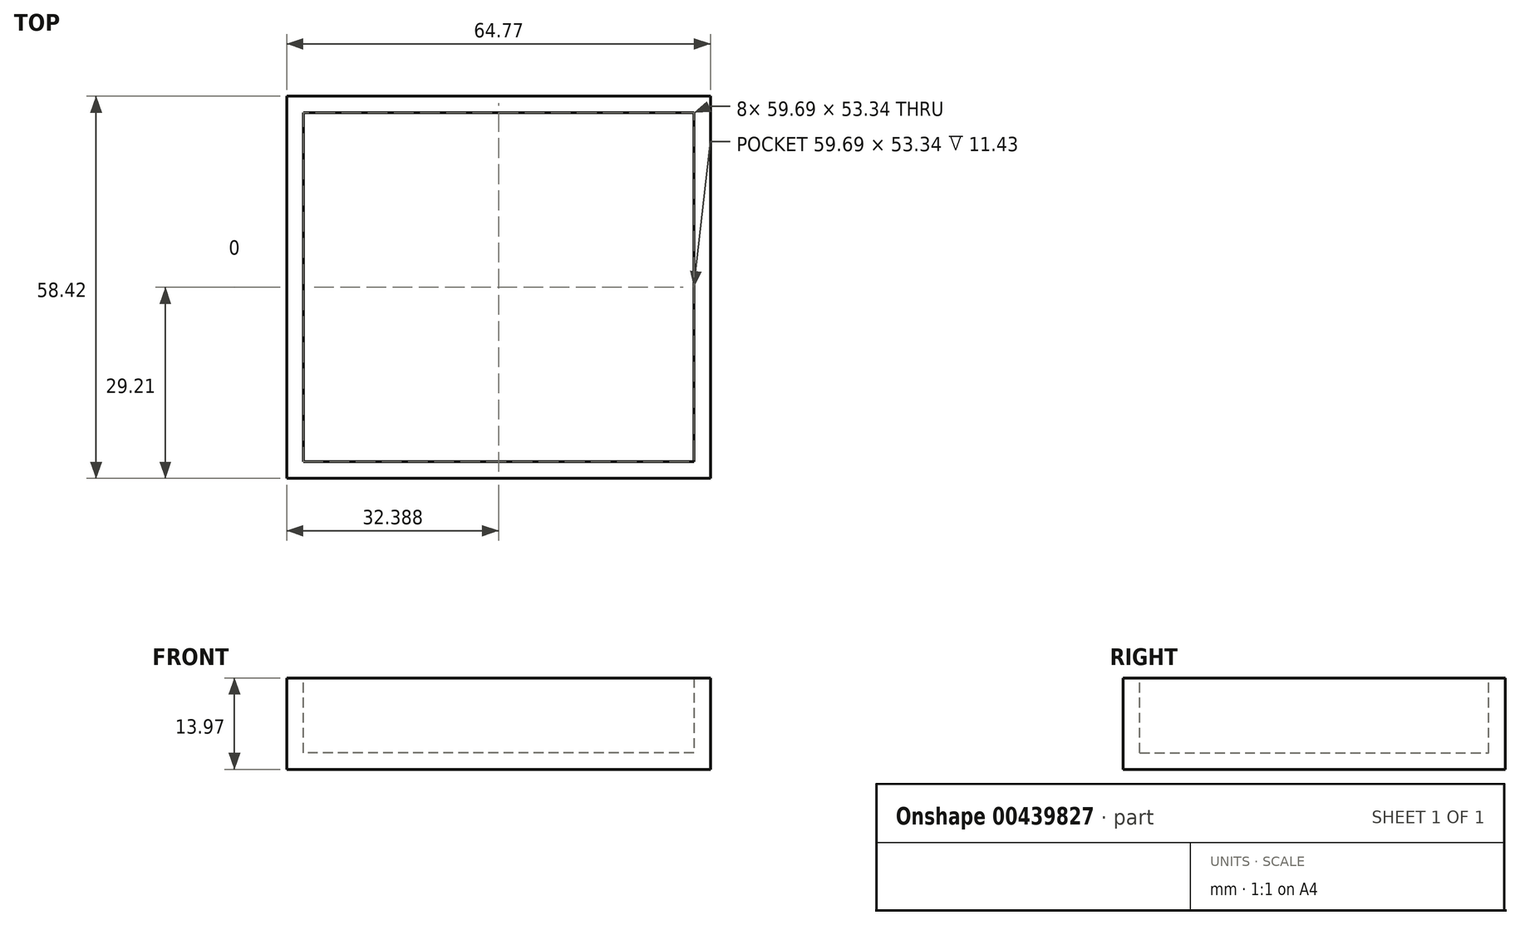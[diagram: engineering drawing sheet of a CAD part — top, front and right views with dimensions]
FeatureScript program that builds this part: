
annotation { "Feature Type Name" : "Feature", "Feature Type Description" : "" }
export const myFeature = defineFeature(function(context is Context, id is Id, definition is map)
    precondition{}
    {
        {
            var Q0;
            Q0=qCreatedBy(makeId("Front.planeOp"),FACE);
            var sketch = newSketch(context, id + "F0", { "sketchPlane" : qUnion([Q0])});
            skLineSegment(sketch, "E0", {"start": v(-52.6, 51.37) * mm, "end": v(-52.6, -62.35) * mm});
            skLineSegment(sketch, "E1", {"start": v(-52.6, -62.35) * mm, "end": v(59.7, -62.35) * mm});
            skLineSegment(sketch, "E2", {"start": v(59.7, -62.35) * mm, "end": v(59.7, 51.37) * mm});
            skLineSegment(sketch, "E3", {"start": v(59.7, 51.37) * mm, "end": v(-52.6, 51.37) * mm});
            skLineSegment(sketch, "E4", {"start": v(-17.56, -42.35) * mm, "end": v(-17.56, -28.38) * mm});
            skLineSegment(sketch, "E5", {"start": v(-17.56, -28.38) * mm, "end": v(47.21, -28.38) * mm});
            skLineSegment(sketch, "E6", {"start": v(47.21, -28.38) * mm, "end": v(47.21, -42.35) * mm});
            skLineSegment(sketch, "E7", {"start": v(47.21, -42.35) * mm, "end": v(-17.56, -42.35) * mm});
            skSolve(sketch);
        }
        {
            var Q0;
            Q0=makeQuery(id+"F0.imprint","IMPRINT",FACE,{"disambiguationData":[TD([[makeQuery(id+"F0.imprint","IMPRINT",EDGE,{"derivedFrom":sQuery(id+"F0.wireOp",EDGE,"E4")}),-1.0]])]});
            extrude(context, id + "F1", {"entities" : qUnion([Q0]), "depth" : 58.42 * mm});
        }
        {
            var Q0;
            Q0=makeQuery(id+"F1.opExtrude","SWEPT_FACE",FACE,{"disambiguationData":[OSD([sQuery(id+"F0.wireOp",EDGE,"E5")])]});
            shell(context, id + "F2", {"entities" : qUnion([Q0]), "thickness" : 2.54 * mm});
        }
    });
